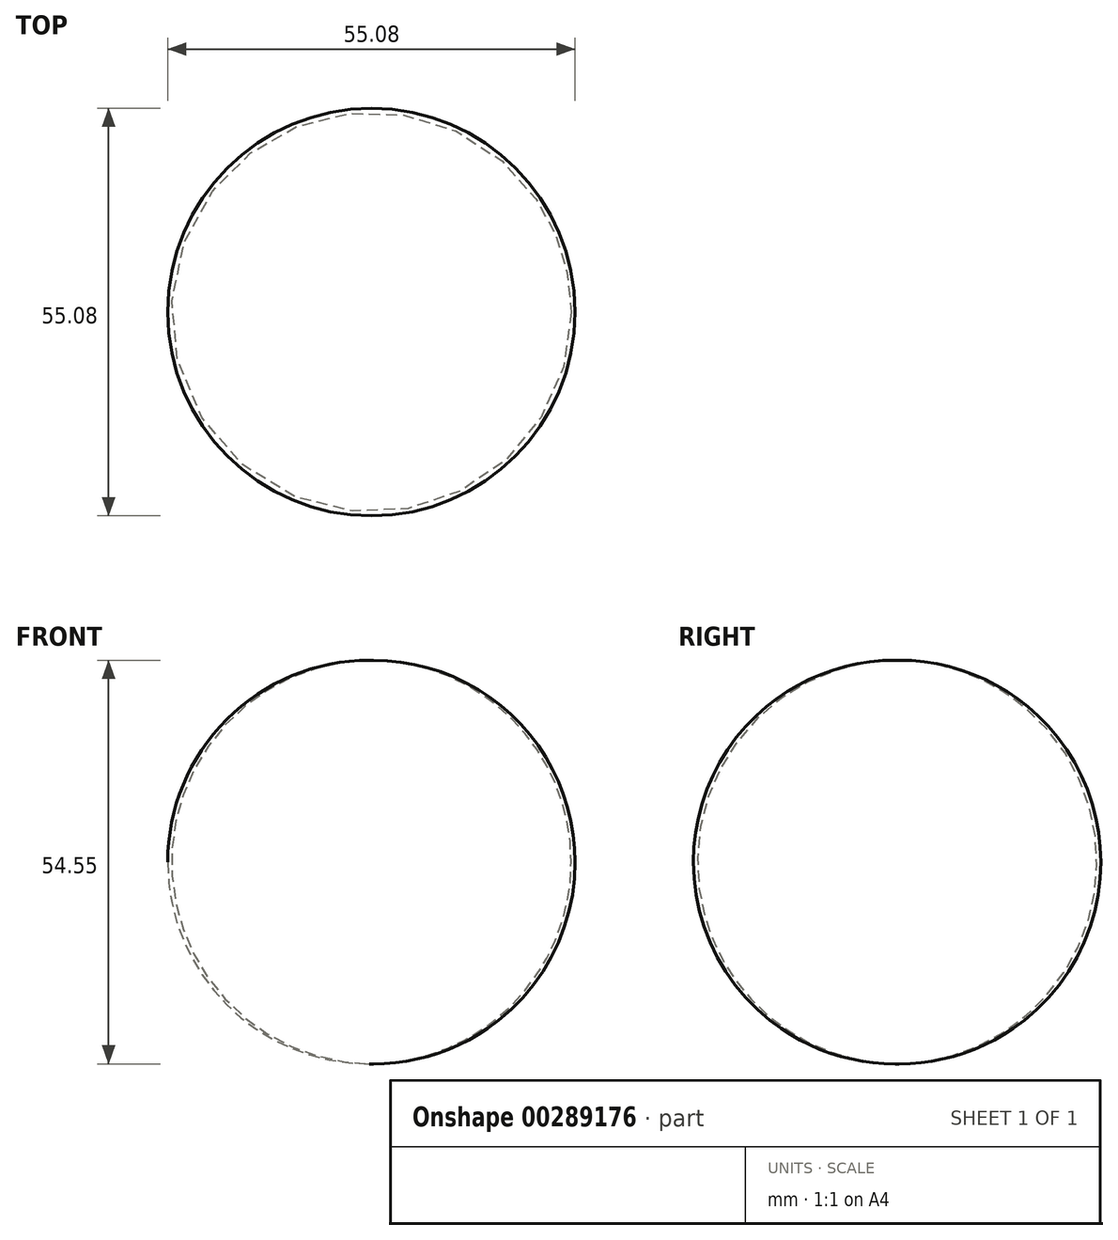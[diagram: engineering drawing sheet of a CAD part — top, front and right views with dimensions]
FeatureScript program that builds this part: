
annotation { "Feature Type Name" : "Feature", "Feature Type Description" : "" }
export const myFeature = defineFeature(function(context is Context, id is Id, definition is map)
    precondition{}
    {
        {
            var Q0;
            Q0=qCreatedBy(makeId("Front.planeOp"),FACE);
            var sketch = newSketch(context, id + "F0", { "sketchPlane" : qUnion([Q0])});
            skLineSegment(sketch, "E0", {"start": v(0, 0) * mm, "end": v(0, 54.55) * mm});
            skArc(sketch, "E1", {"start": v(0, 0) * mm, "mid": v(27.54, 27.27) * mm, "end": v(0, 54.55) * mm});
            skSolve(sketch);
        }
        {
            var Q0;
            Q0 = qSketchRegion(id + "F0", true);
            var Q1;
            Q1=sQuery(id+"F0.wireOp",EDGE,"E0");
            revolve(context, id + "F1", {"entities" : qUnion([Q0]), "axis" : qUnion([Q1]), "revolveType" : RevolveType.FULL});
        }
    });
